# Revit family: New Dritta 90_95800
name_source: partatom
category: Equipamento especial
revit_build: Autodesk Revit 2016 (Build: 20150220_1215(x64)
units: mm (PartAtom-declared; Revit-internal decimal feet)

## family parameters
Compartilhado = Não
Corte com vazios quando carregados = Não
Cota do conector redondo = Utilizar diâmetro
Hospedeiro = Parede
Número OmniClass = 23.40.40.14.17.11
Ponto de cálculo do ambiente = Não
Sempre na vertical = Sim
Tipo de parte = Normal
Título OmniClass = Cookers, Ovens, Stoves

## types (2) — shared parameters
Atendimento ao Cliente = http://www.tramontina.com.br
Classe da Construção = CLASSE I
Descrição = Coifa New Dritta 90
Desenvolvedor da Biblioteca = Factory Cursos e Desenvolvimento
Dimensoes (mm) = 500x 900x  540-1020
Disjuntor Termomagnético = 10 A
Fabricante = Tramontina
Filtro de Aluminio = 3
Filtro de Carvao Ativado = 2
Frequência = 60 Hz
Grau de Proteção = IPXO
Iluminação = 2 x 1,5 W - 12 V - Lâmpadas LED
Linha = Dritta
Numero de Velocidades = 3
Nível de Ruído = 64 dB (A) - cfe. Norma EN 60704
Peso Bruto (Kg) = 19.8
Peso Líquido (Kg) = 16.7
Potência Elétrica = 225 W
Potência do Motor = 220 W
Produto = Coifa New Dritta 90
Segmento = Residencial
Site do Desenvolvedor = www.factorycursos.com.br
URL = www.tramontina.com.br
Vazão Máxima = 620 m³/h - cfe. Norma IEC 61591

## per-type parameters (varying)
| type | Código da Peça | Modelo | Tensão |
| 220 Volts | 95800/004 | 95800/004 | 220 V |
| 110 | 95800/003 | 95800/003 | 110 V |

## geometry (parser evidence)
native form markers: Sweep x2
no freeform markers — native parametric forms only
